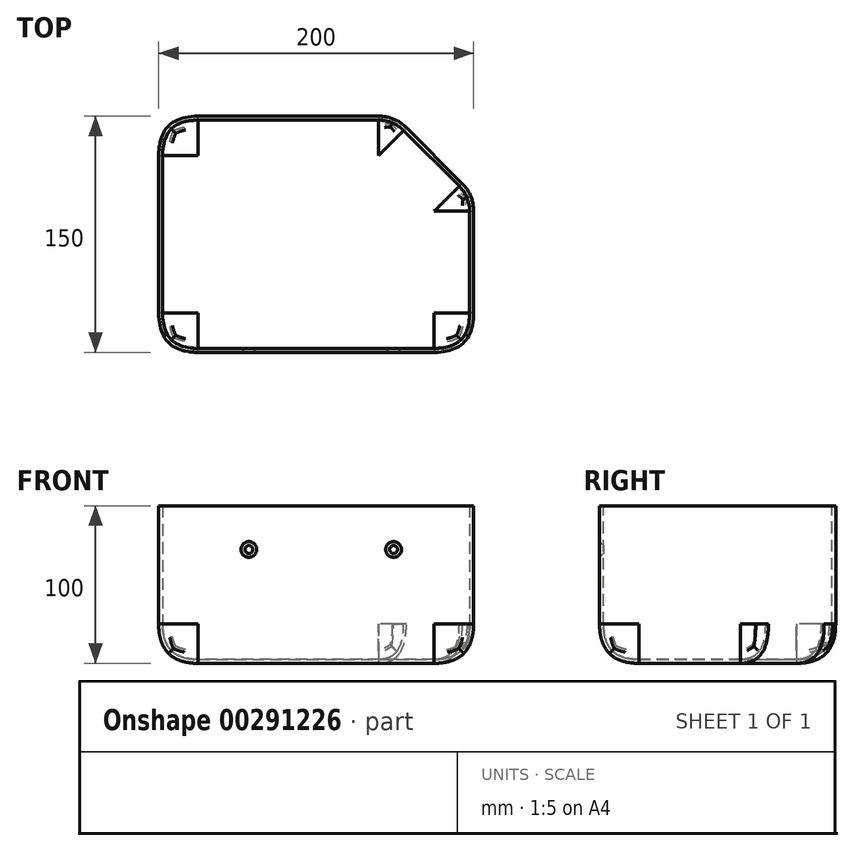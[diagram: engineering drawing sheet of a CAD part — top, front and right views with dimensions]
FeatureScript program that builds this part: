
annotation { "Feature Type Name" : "Feature", "Feature Type Description" : "" }
export const myFeature = defineFeature(function(context is Context, id is Id, definition is map)
    precondition{}
    {
        {
            var Q0;
            Q0=qCreatedBy(makeId("Top.planeOp"),FACE);
            var sketch = newSketch(context, id + "F0", { "sketchPlane" : qUnion([Q0])});
            skLineSegment(sketch, "E0.bottom", {"start": v(100, 75) * mm, "end": v(-100, 75) * mm});
            skLineSegment(sketch, "E0.top", {"start": v(100, -75) * mm, "end": v(-100, -75) * mm});
            skLineSegment(sketch, "E0.left", {"start": v(100, 75) * mm, "end": v(100, -75) * mm});
            skLineSegment(sketch, "E0.right", {"start": v(-100, 75) * mm, "end": v(-100, -75) * mm});
            skPoint(sketch, "E0.middle", {"position": v(0, 0) * mm});
            skSolve(sketch);
        }
        {
            var Q0;
            Q0=makeQuery(id+"F0.imprint","IMPRINT",FACE,{"disambiguationData":[TD([[makeQuery(id+"F0.imprint","IMPRINT",EDGE,{"derivedFrom":sQuery(id+"F0.wireOp",EDGE,"E0.bottom")}),1.0]])]});
            extrude(context, id + "F1", {"entities" : qUnion([Q0]), "depth" : 100 * mm});
        }
        {
            var Q0;
            Q0=makeQuery(id+"F1.opExtrude","SWEPT_EDGE",EDGE,{"disambiguationData":[OSD([sQuery(id+"F0.wireOp",EDGE,"E0.bottom"),sQuery(id+"F0.wireOp",EDGE,"E0.left")])]});
            chamfer(context, id + "F2", {"entities" : qUnion([Q0]), "width" : 50 * mm, "tangentPropagation" : true});
        }
        {
            var Q0;
            Q0=makeQuery(id+"F1.opExtrude","SWEPT_EDGE",EDGE,{"disambiguationData":[OSD([sQuery(id+"F0.wireOp",EDGE,"E0.top"),sQuery(id+"F0.wireOp",EDGE,"E0.right")])]});
            var Q1;
            Q1=makeQuery(id+"F1.opExtrude","SWEPT_EDGE",EDGE,{"disambiguationData":[OSD([sQuery(id+"F0.wireOp",EDGE,"E0.bottom"),sQuery(id+"F0.wireOp",EDGE,"E0.right")])]});
            var Q2;
            Q2=makeQuery(id+"F1.opExtrude","SWEPT_EDGE",EDGE,{"disambiguationData":[OSD([sQuery(id+"F0.wireOp",EDGE,"E0.top"),sQuery(id+"F0.wireOp",EDGE,"E0.left")])]});
            var Q3;
            Q3=makeQuery(id+"F1.opExtrude","CAP_EDGE",EDGE,{"disambiguationData":[OSD([sQuery(id+"F0.wireOp",EDGE,"E0.top")])],"isStart":true});
            var Q4;
            Q4=makeQuery(id+"F1.opExtrude","CAP_EDGE",EDGE,{"disambiguationData":[OSD([sQuery(id+"F0.wireOp",EDGE,"E0.right")])],"isStart":true});
            var Q5;
            {var subQ0=sQuery(id+"F0.wireOp",EDGE,"E0.left");Q5=makeQuery(id+"F2.opChamfer","BLEND_EDGE",EDGE,{"blendedFrom":[makeQuery(id+"F1.opExtrude","SWEPT_EDGE",EDGE,{"disambiguationData":[OSD([sQuery(id+"F0.wireOp",EDGE,"E0.bottom"),subQ0])]}),makeQuery(id+"F1.opExtrude","SWEPT_FACE",FACE,{"disambiguationData":[OSD([subQ0])]})],"blendedInto":[makeQuery(id+"F1.opExtrude","SWEPT_FACE",FACE,{"disambiguationData":[OSD([subQ0])]})]});}
            var Q6;
            {var subQ0=sQuery(id+"F0.wireOp",EDGE,"E0.bottom");Q6=makeQuery(id+"F2.opChamfer","BLEND_EDGE",EDGE,{"blendedFrom":[makeQuery(id+"F1.opExtrude","SWEPT_EDGE",EDGE,{"disambiguationData":[OSD([subQ0,sQuery(id+"F0.wireOp",EDGE,"E0.left")])]}),makeQuery(id+"F1.opExtrude","SWEPT_FACE",FACE,{"disambiguationData":[OSD([subQ0])]})],"blendedInto":[makeQuery(id+"F1.opExtrude","SWEPT_FACE",FACE,{"disambiguationData":[OSD([subQ0])]})]});}
            var Q7;
            {var subQ0=sQuery(id+"F0.wireOp",EDGE,"E0.left");var subQ1=sQuery(id+"F0.wireOp",EDGE,"E0.bottom");Q7=makeQuery(id+"F2.opChamfer","BLEND_EDGE",EDGE,{"blendedFrom":[makeQuery(id+"F1.opExtrude","SWEPT_EDGE",EDGE,{"disambiguationData":[OSD([subQ1,subQ0])]}),makeQuery(id+"F1.opExtrude","CAP_FACE",FACE,{"disambiguationData":[OSD([subQ1,sQuery(id+"F0.wireOp",EDGE,"E0.top"),subQ0,sQuery(id+"F0.wireOp",EDGE,"E0.right")])],"isStart":true})],"blendedInto":[makeQuery(id+"F1.opExtrude","CAP_FACE",FACE,{"disambiguationData":[OSD([subQ1,sQuery(id+"F0.wireOp",EDGE,"E0.top"),subQ0,sQuery(id+"F0.wireOp",EDGE,"E0.right")])],"isStart":true})]});}
            var Q8;
            Q8=makeQuery(id+"F1.opExtrude","CAP_EDGE",EDGE,{"disambiguationData":[OSD([sQuery(id+"F0.wireOp",EDGE,"E0.left")])],"isStart":true});
            var Q9;
            Q9=makeQuery(id+"F1.opExtrude","CAP_FACE",FACE,{"disambiguationData":[OSD([sQuery(id+"F0.wireOp",EDGE,"E0.bottom"),sQuery(id+"F0.wireOp",EDGE,"E0.top"),sQuery(id+"F0.wireOp",EDGE,"E0.left"),sQuery(id+"F0.wireOp",EDGE,"E0.right")])],"isStart":true});
            fillet(context, id + "F3", {"entities" : qUnion([Q0, Q1, Q2, Q3, Q4, Q5, Q6, Q7, Q8, Q9]), "radius" : 25 * mm, "tangentPropagation" : true, "rho" : 0.5, "crossSection" : FilletCrossSection.CONIC, "allowEdgeOverflow" : false});
        }
        {
            var Q0;
            Q0=makeQuery(id+"F1.opExtrude","CAP_FACE",FACE,{"disambiguationData":[OSD([sQuery(id+"F0.wireOp",EDGE,"E0.bottom"),sQuery(id+"F0.wireOp",EDGE,"E0.top"),sQuery(id+"F0.wireOp",EDGE,"E0.left"),sQuery(id+"F0.wireOp",EDGE,"E0.right")])],"isStart":false});
            shell(context, id + "F4", {"entities" : qUnion([Q0]), "thickness" : 2.5 * mm});
        }
        {
            var Q0;
            Q0=makeQuery(id+"F1.opExtrude","SWEPT_FACE",FACE,{"disambiguationData":[OSD([sQuery(id+"F0.wireOp",EDGE,"E0.top")])]});
            var sketch = newSketch(context, id + "F5", { "sketchPlane" : qUnion([Q0])});
            skPoint(sketch, "E1", {"position": v(-42.73, 72.3) * mm});
            skPoint(sketch, "E2", {"position": v(49.2, 72.3) * mm});
            skSolve(sketch);
        }
        {
            var Q0;
            Q0=sQuery(id+"F5.wireOp",VERTEX,"E1");
            var Q1;
            Q1=sQuery(id+"F5.wireOp",VERTEX,"E2");
            var Q2;
            Q2=makeQuery(id+"F1.opExtrude","SWEPT_BODY",BODY,{"disambiguationData":[OSD([sQuery(id+"F0.wireOp",EDGE,"E0.bottom"),sQuery(id+"F0.wireOp",EDGE,"E0.top"),sQuery(id+"F0.wireOp",EDGE,"E0.left"),sQuery(id+"F0.wireOp",EDGE,"E0.right")])]});
            hole(context, id + "F6", {"style" : HoleStyle.C_SINK, "endStyle" : HoleEndStyle.BLIND, "holeDiameter" : 5 * mm, "cSinkDiameter" : 10 * mm, "cSinkAngle" : 90 * degree, "holeDepth" : 12 * mm, "tappedDepth" : 12 * mm, "tapClearance" : 3, "locations" : qUnion([Q0, Q1]), "scope" : qUnion([Q2])});
        }
    });
